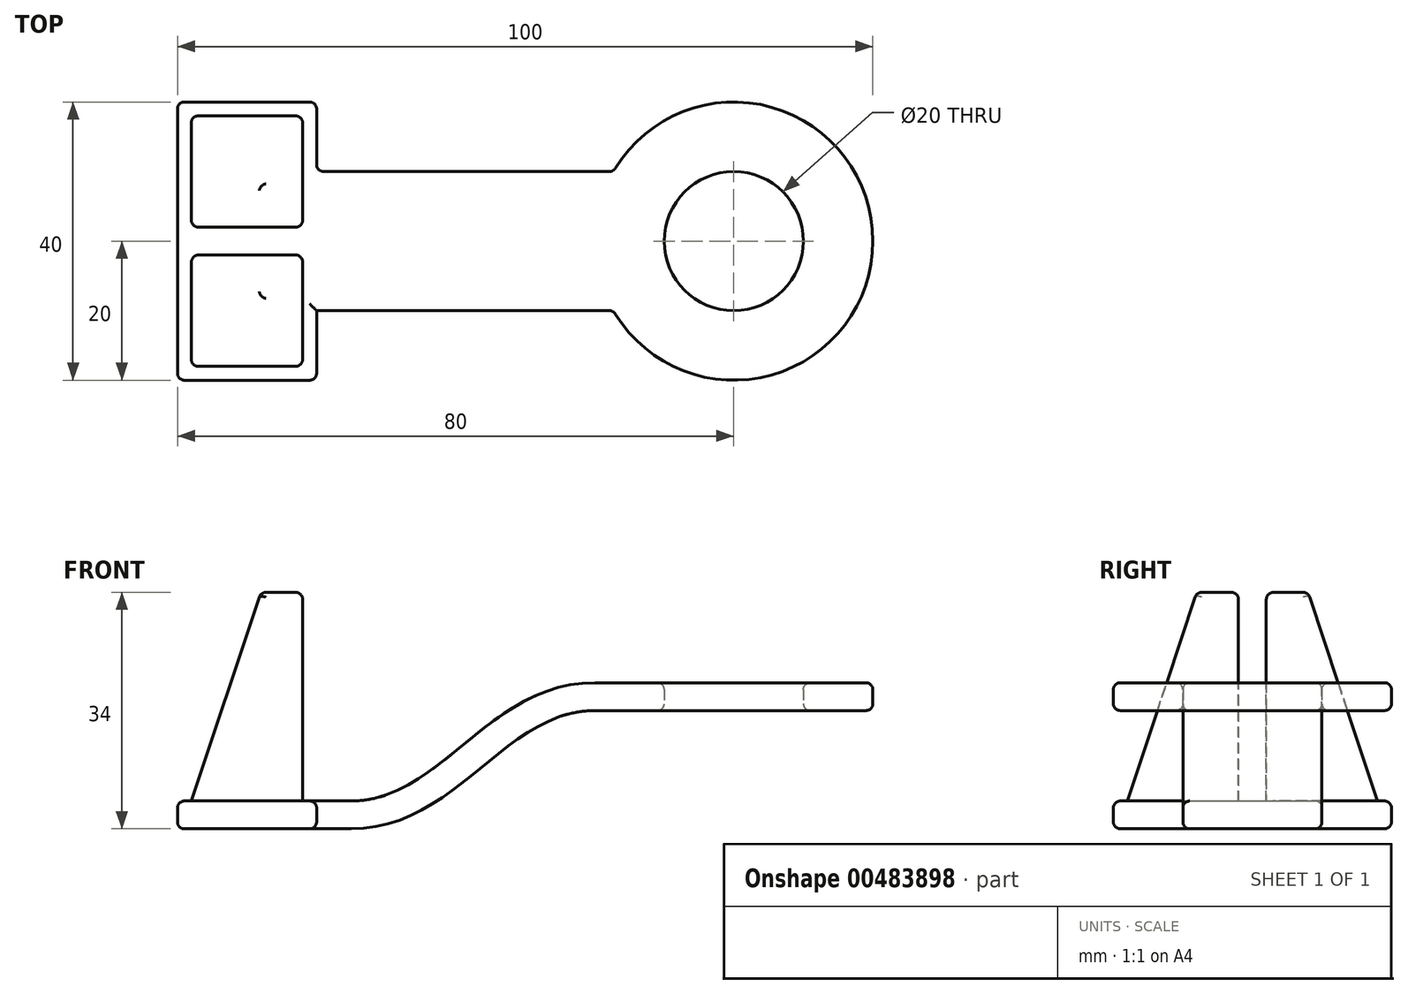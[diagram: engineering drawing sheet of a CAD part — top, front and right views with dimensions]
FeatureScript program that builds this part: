
annotation { "Feature Type Name" : "Feature", "Feature Type Description" : "" }
export const myFeature = defineFeature(function(context is Context, id is Id, definition is map)
    precondition{}
    {
        {
            var Q0;
            Q0=qCreatedBy(makeId("Front.planeOp"),FACE);
            var sketch = newSketch(context, id + "F0", { "sketchPlane" : qUnion([Q0])});
            skLineSegment(sketch, "E0.bottom", {"start": v(10, -2) * mm, "end": v(-10, -2) * mm});
            skLineSegment(sketch, "E0.top", {"start": v(10, 2) * mm, "end": v(-10, 2) * mm});
            skLineSegment(sketch, "E0.left", {"start": v(10, -2) * mm, "end": v(10, 2) * mm});
            skLineSegment(sketch, "E0.right", {"start": v(-10, -2) * mm, "end": v(-10, 2) * mm});
            skPoint(sketch, "E0.middle", {"position": v(0, 0) * mm});
            skLineSegment(sketch, "E1.bottom", {"start": v(56, 15) * mm, "end": v(50, 15) * mm});
            skLineSegment(sketch, "E1.top", {"start": v(56, 19) * mm, "end": v(50, 19) * mm});
            skLineSegment(sketch, "E1.left", {"start": v(56, 15) * mm, "end": v(56, 19) * mm});
            skLineSegment(sketch, "E1.right", {"start": v(50, 15) * mm, "end": v(50, 19) * mm});
            skPoint(sketch, "E1.middle", {"position": v(53, 17) * mm});
            skLineSegment(sketch, "E2.0", {"start": v(70, 15) * mm, "end": v(70, 19) * mm, "construction": true});
            skLineSegment(sketch, "E3.bottom", {"start": v(80, 15) * mm, "end": v(90, 15) * mm});
            skLineSegment(sketch, "E3.top", {"start": v(80, 19) * mm, "end": v(90, 19) * mm});
            skLineSegment(sketch, "E3.left", {"start": v(80, 15) * mm, "end": v(80, 19) * mm});
            skLineSegment(sketch, "E3.right", {"start": v(90, 15) * mm, "end": v(90, 19) * mm});
            skLineSegment(sketch, "E4.bottom", {"start": v(10, -2) * mm, "end": v(15, -2) * mm});
            skLineSegment(sketch, "E4.top", {"start": v(10, 2) * mm, "end": v(15, 2) * mm});
            skLineSegment(sketch, "E4.right", {"start": v(15, -2) * mm, "end": v(15, 2) * mm});
            skFitSpline(sketch, "E5", {"points": [v(15, 2) * mm, v(50, 19) * mm], "startDerivative": vector(38.92, 0) * mm, "endDerivative": vector(46.09, 0) * mm});
            skFitSpline(sketch, "E6", {"points": [v(15, -2) * mm, v(50, 15) * mm], "startDerivative": vector(45.29, 0) * mm, "endDerivative": vector(38.92, 0) * mm});
            skSolve(sketch);
        }
        {
            var Q0;
            Q0=makeQuery(id+"F0.imprint","IMPRINT",FACE,{"disambiguationData":[TD([[makeQuery(id+"F0.imprint","IMPRINT",EDGE,{"derivedFrom":sQuery(id+"F0.wireOp",EDGE,"E3.bottom")}),1.0]])]});
            var Q1;
            Q1=sQuery(id+"F0.wireOp",EDGE,"E2.0");
            revolve(context, id + "F1", {"entities" : qUnion([Q0]), "axis" : qUnion([Q1]), "revolveType" : RevolveType.FULL});
        }
        {
            var Q0;
            Q0=makeQuery(id+"F0.imprint","IMPRINT",FACE,{"disambiguationData":[TD([[makeQuery(id+"F0.imprint","IMPRINT",EDGE,{"derivedFrom":sQuery(id+"F0.wireOp",EDGE,"E1.bottom")}),-1.0]])]});
            extrude(context, id + "F2", {"entities" : qUnion([Q0]), "operationType" : NewBodyOperationType.ADD, "endBound" : BoundingType.SYMMETRIC, "depth" : 20 * mm, "offsetDistance" : 25 * mm});
        }
        {
            var Q0;
            Q0=makeQuery(id+"F0.imprint","IMPRINT",FACE,{"disambiguationData":[TD([[makeQuery(id+"F0.imprint","IMPRINT",EDGE,{"derivedFrom":sQuery(id+"F0.wireOp",EDGE,"E0.bottom")}),-1.0]])]});
            extrude(context, id + "F3", {"entities" : qUnion([Q0]), "operationType" : NewBodyOperationType.ADD, "endBound" : BoundingType.SYMMETRIC, "depth" : 40 * mm, "offsetDistance" : 25 * mm});
        }
        {
            var Q0;
            Q0=makeQuery(id+"F0.imprint","IMPRINT",FACE,{"disambiguationData":[TD([[makeQuery(id+"F0.imprint","IMPRINT",EDGE,{"derivedFrom":sQuery(id+"F0.wireOp",EDGE,"E1.right")}),1.0]])]});
            extrude(context, id + "F4", {"entities" : qUnion([Q0]), "operationType" : NewBodyOperationType.ADD, "endBound" : BoundingType.SYMMETRIC, "depth" : 20 * mm, "offsetDistance" : 25 * mm});
        }
        {
            var Q0;
            Q0=makeQuery(id+"F0.imprint","IMPRINT",FACE,{"disambiguationData":[TD([[makeQuery(id+"F0.imprint","IMPRINT",EDGE,{"derivedFrom":sQuery(id+"F0.wireOp",EDGE,"E4.bottom")}),1.0]])]});
            extrude(context, id + "F5", {"entities" : qUnion([Q0]), "operationType" : NewBodyOperationType.ADD, "endBound" : BoundingType.SYMMETRIC, "depth" : 20 * mm, "offsetDistance" : 25 * mm});
        }
        {
            var Q0;
            Q0=makeQuery(id+"F3.opExtrude","SWEPT_FACE",FACE,{"disambiguationData":[OSD([sQuery(id+"F0.wireOp",EDGE,"E0.top")])]});
            var sketch = newSketch(context, id + "F6", { "sketchPlane" : qUnion([Q0])});
            skLineSegment(sketch, "E7.bottom", {"start": v(-8, 18) * mm, "end": v(8, 18) * mm});
            skLineSegment(sketch, "E7.top", {"start": v(-8, 2) * mm, "end": v(8, 2) * mm});
            skLineSegment(sketch, "E7.left", {"start": v(-8, 18) * mm, "end": v(-8, 2) * mm});
            skLineSegment(sketch, "E7.right", {"start": v(8, 18) * mm, "end": v(8, 2) * mm});
            skLineSegment(sketch, "E8.MirrorCS", {"start": v(-8, -2) * mm, "end": v(8, -2) * mm});
            skLineSegment(sketch, "E9.MirrorCS", {"start": v(8, -18) * mm, "end": v(8, -2) * mm});
            skLineSegment(sketch, "E10.MirrorCS", {"start": v(-8, -18) * mm, "end": v(8, -18) * mm});
            skLineSegment(sketch, "E11.MirrorCS", {"start": v(-8, -18) * mm, "end": v(-8, -2) * mm});
            skSolve(sketch);
        }
        {
            var Q0;
            Q0=makeQuery(id+"F3.opExtrude","SWEPT_FACE",FACE,{"disambiguationData":[OSD([sQuery(id+"F0.wireOp",EDGE,"E0.top")])]});
            cPlane(context, id + "F7", {"entities" : qUnion([Q0]), "cplaneType" : CPlaneType.OFFSET, "offset" : 30 * mm, "width" : 150 * mm, "height" : 150 * mm});
        }
        {
            var Q0;
            Q0=qCreatedBy(id+"F7.planeOp",FACE);
            var sketch = newSketch(context, id + "F8", { "sketchPlane" : qUnion([Q0])});
            skLineSegment(sketch, "E12.bottom", {"start": v(8, 2) * mm, "end": v(2, 2) * mm});
            skLineSegment(sketch, "E12.top", {"start": v(8, 8) * mm, "end": v(2, 8) * mm});
            skLineSegment(sketch, "E12.left", {"start": v(2, 8) * mm, "end": v(2, 2) * mm});
            skLineSegment(sketch, "E12.right", {"start": v(8, 8) * mm, "end": v(8, 2) * mm});
            skLineSegment(sketch, "E13.MirrorCS", {"start": v(8, -2) * mm, "end": v(2, -2) * mm});
            skLineSegment(sketch, "E14.MirrorCS", {"start": v(8, -8) * mm, "end": v(8, -2) * mm});
            skLineSegment(sketch, "E15.MirrorCS", {"start": v(8, -8) * mm, "end": v(2, -8) * mm});
            skLineSegment(sketch, "E16.MirrorCS", {"start": v(2, -8) * mm, "end": v(2, -2) * mm});
            skSolve(sketch);
        }
        {
            var Q1;
            Q1=makeQuery(id+"F6.imprint","IMPRINT",FACE,{"disambiguationData":[TD([[makeQuery(id+"F6.imprint","IMPRINT",EDGE,{"derivedFrom":sQuery(id+"F6.wireOp",EDGE,"E8.MirrorCS")}),-1.0]])]});
            var Q2;
            Q2=makeQuery(id+"F8.imprint","IMPRINT",FACE,{"disambiguationData":[TD([[makeQuery(id+"F8.imprint","IMPRINT",EDGE,{"derivedFrom":sQuery(id+"F8.wireOp",EDGE,"E13.MirrorCS")}),1.0]])]});
            loft(context, id + "F9", {"operationType" : NewBodyOperationType.ADD, "sheetProfilesArray" : [{ "sheetProfileEntities" : qUnion([Q1]) }, { "sheetProfileEntities" : qUnion([Q2]) }]});
        }
        {
            var Q1;
            Q1=makeQuery(id+"F6.imprint","IMPRINT",FACE,{"disambiguationData":[TD([[makeQuery(id+"F6.imprint","IMPRINT",EDGE,{"derivedFrom":sQuery(id+"F6.wireOp",EDGE,"E7.bottom")}),-1.0]])]});
            var Q2;
            Q2=makeQuery(id+"F8.imprint","IMPRINT",FACE,{"disambiguationData":[TD([[makeQuery(id+"F8.imprint","IMPRINT",EDGE,{"derivedFrom":sQuery(id+"F8.wireOp",EDGE,"E12.bottom")}),-1.0]])]});
            loft(context, id + "F10", {"operationType" : NewBodyOperationType.ADD, "sheetProfilesArray" : [{ "sheetProfileEntities" : qUnion([Q1]) }, { "sheetProfileEntities" : qUnion([Q2]) }]});
        }
        {
            var Q0;
            Q0=makeQuery(id+"F3.opExtrude","CAP_EDGE",EDGE,{"disambiguationData":[OSD([sQuery(id+"F0.wireOp",EDGE,"E0.bottom")])],"isStart":false});
            var Q1;
            Q1=makeQuery(id+"F3.opExtrude","SWEPT_EDGE",EDGE,{"disambiguationData":[OSD([sQuery(id+"F0.wireOp",EDGE,"E0.bottom"),sQuery(id+"F0.wireOp",EDGE,"E0.right")])]});
            var Q2;
            Q2=makeQuery(id+"F3.opExtrude","CAP_EDGE",EDGE,{"disambiguationData":[OSD([sQuery(id+"F0.wireOp",EDGE,"E0.bottom")])],"isStart":true});
            var Q3;
            {var subQ0=sQuery(id+"F0.wireOp",EDGE,"E0.left");var subQ1=sQuery(id+"F0.wireOp",EDGE,"E0.bottom");var subQ2=sQuery(id+"F0.wireOp",EDGE,"E1.right");var subQ4=sQuery(id+"F0.wireOp",EDGE,"E4.bottom");Q3=makeQuery(id+"F5.boolean.opBoolean","SPLIT",EDGE,{"disambiguationData":[TD([makeQuery(id+"F2.opExtrude","CAP_FACE",FACE,{"disambiguationData":[OSD([sQuery(id+"F0.wireOp",EDGE,"E1.bottom"),sQuery(id+"F0.wireOp",EDGE,"E1.top"),sQuery(id+"F0.wireOp",EDGE,"E1.left"),subQ2])],"isStart":true})])],"derivedFrom":makeQuery(id+"F3.opExtrude","SWEPT_EDGE",EDGE,{"disambiguationData":[OSD([subQ1,subQ4,subQ0])]})});}
            var Q4;
            {var subQ0=sQuery(id+"F0.wireOp",EDGE,"E0.left");var subQ1=sQuery(id+"F0.wireOp",EDGE,"E0.bottom");var subQ2=sQuery(id+"F0.wireOp",EDGE,"E1.right");var subQ4=sQuery(id+"F0.wireOp",EDGE,"E4.bottom");Q4=makeQuery(id+"F5.boolean.opBoolean","SPLIT",EDGE,{"disambiguationData":[TD([makeQuery(id+"F2.opExtrude","CAP_FACE",FACE,{"disambiguationData":[OSD([sQuery(id+"F0.wireOp",EDGE,"E1.bottom"),sQuery(id+"F0.wireOp",EDGE,"E1.top"),sQuery(id+"F0.wireOp",EDGE,"E1.left"),subQ2])],"isStart":false})])],"derivedFrom":makeQuery(id+"F3.opExtrude","SWEPT_EDGE",EDGE,{"disambiguationData":[OSD([subQ1,subQ4,subQ0])]})});}
            fillet(context, id + "F11", {"entities" : qUnion([Q0, Q1, Q2, Q3, Q4]), "radius" : 1 * mm, "tangentPropagation" : true, "allowEdgeOverflow" : false});
        }
        {
            var Q0;
            Q0=makeQuery(id+"F3.opExtrude","CAP_EDGE",EDGE,{"disambiguationData":[OSD([sQuery(id+"F0.wireOp",EDGE,"E0.top")])],"isStart":false});
            var Q1;
            {var subQ0=sQuery(id+"F0.wireOp",EDGE,"E0.top");var subQ2=sQuery(id+"F0.wireOp",EDGE,"E1.right");var subQ3=sQuery(id+"F0.wireOp",EDGE,"E0.left");var subQ4=sQuery(id+"F0.wireOp",EDGE,"E4.top");Q1=makeQuery(id+"F5.boolean.opBoolean","SPLIT",EDGE,{"disambiguationData":[TD([makeQuery(id+"F2.opExtrude","CAP_FACE",FACE,{"disambiguationData":[OSD([sQuery(id+"F0.wireOp",EDGE,"E1.bottom"),sQuery(id+"F0.wireOp",EDGE,"E1.top"),sQuery(id+"F0.wireOp",EDGE,"E1.left"),subQ2])],"isStart":false})])],"derivedFrom":makeQuery(id+"F3.opExtrude","SWEPT_EDGE",EDGE,{"disambiguationData":[OSD([subQ0,subQ4,subQ3])]})});}
            var Q2;
            Q2=makeQuery(id+"F3.opExtrude","SWEPT_EDGE",EDGE,{"disambiguationData":[OSD([sQuery(id+"F0.wireOp",EDGE,"E0.top"),sQuery(id+"F0.wireOp",EDGE,"E0.right")])]});
            var Q3;
            Q3=makeQuery(id+"F5.opExtrude","CAP_EDGE",EDGE,{"disambiguationData":[OSD([sQuery(id+"F0.wireOp",EDGE,"E4.top")])],"isStart":false});
            var Q4;
            Q4=makeQuery(id+"F5.opExtrude","CAP_EDGE",EDGE,{"disambiguationData":[OSD([sQuery(id+"F0.wireOp",EDGE,"E4.top")])],"isStart":true});
            var Q5;
            {var subQ0=sQuery(id+"F0.wireOp",EDGE,"E0.left");var subQ1=sQuery(id+"F0.wireOp",EDGE,"E0.top");var subQ2=sQuery(id+"F0.wireOp",EDGE,"E4.top");var subQ3=sQuery(id+"F0.wireOp",EDGE,"E1.right");Q5=makeQuery(id+"F5.boolean.opBoolean","SPLIT",EDGE,{"disambiguationData":[TD([makeQuery(id+"F2.opExtrude","CAP_FACE",FACE,{"disambiguationData":[OSD([sQuery(id+"F0.wireOp",EDGE,"E1.bottom"),sQuery(id+"F0.wireOp",EDGE,"E1.top"),sQuery(id+"F0.wireOp",EDGE,"E1.left"),subQ3])],"isStart":true})])],"derivedFrom":makeQuery(id+"F3.opExtrude","SWEPT_EDGE",EDGE,{"disambiguationData":[OSD([subQ1,subQ2,subQ0])]})});}
            var Q6;
            Q6=makeQuery(id+"F3.opExtrude","CAP_EDGE",EDGE,{"disambiguationData":[OSD([sQuery(id+"F0.wireOp",EDGE,"E0.top")])],"isStart":true});
            var Q7;
            Q7=makeQuery(id+"F3.opExtrude","CAP_EDGE",EDGE,{"disambiguationData":[OSD([sQuery(id+"F0.wireOp",EDGE,"E0.left")])],"isStart":false});
            var Q8;
            Q8=makeQuery(id+"F3.opExtrude","CAP_EDGE",EDGE,{"disambiguationData":[OSD([sQuery(id+"F0.wireOp",EDGE,"E0.right")])],"isStart":false});
            var Q9;
            Q9=makeQuery(id+"F3.opExtrude","CAP_EDGE",EDGE,{"disambiguationData":[OSD([sQuery(id+"F0.wireOp",EDGE,"E0.left")])],"isStart":true});
            var Q10;
            Q10=makeQuery(id+"F5.opExtrude","CAP_EDGE",EDGE,{"disambiguationData":[OSD([sQuery(id+"F0.wireOp",EDGE,"E4.bottom")])],"isStart":false});
            var Q11;
            Q11=makeQuery(id+"F5.opExtrude","CAP_EDGE",EDGE,{"disambiguationData":[OSD([sQuery(id+"F0.wireOp",EDGE,"E0.left")])],"isStart":false});
            var Q12;
            Q12=makeQuery(id+"F3.opExtrude","CAP_EDGE",EDGE,{"disambiguationData":[OSD([sQuery(id+"F0.wireOp",EDGE,"E0.right")])],"isStart":true});
            var Q13;
            Q13=makeQuery(id+"F5.opExtrude","CAP_EDGE",EDGE,{"disambiguationData":[OSD([sQuery(id+"F0.wireOp",EDGE,"E0.left")])],"isStart":true});
            var Q14;
            Q14=makeQuery(id+"F5.opExtrude","CAP_EDGE",EDGE,{"disambiguationData":[OSD([sQuery(id+"F0.wireOp",EDGE,"E4.bottom")])],"isStart":true});
            fillet(context, id + "F12", {"entities" : qUnion([Q0, Q1, Q2, Q3, Q4, Q5, Q6, Q7, Q8, Q9, Q10, Q11, Q12, Q13, Q14]), "radius" : 1 * mm, "tangentPropagation" : true, "allowEdgeOverflow" : false});
        }
        {
            var Q0;
            Q0=makeQuery(id+"F9.opLoft","MID_CAP_EDGE",EDGE,{"disambiguationData":[OSD([sQuery(id+"F6.wireOp",EDGE,"E9.MirrorCS"),sQuery(id+"F6.wireOp",EDGE,"E10.MirrorCS"),sQuery(id+"F6.wireOp",EDGE,"E11.MirrorCS")])],"capPos":0.0});
            var Q1;
            Q1=makeQuery(id+"F9.opLoft","SWEPT_EDGE",EDGE,{"disambiguationData":[OSD([sQuery(id+"F6.wireOp",EDGE,"E10.MirrorCS"),sQuery(id+"F6.wireOp",EDGE,"E11.MirrorCS"),sQuery(id+"F8.wireOp",EDGE,"E15.MirrorCS"),sQuery(id+"F8.wireOp",EDGE,"E16.MirrorCS")])]});
            var Q2;
            Q2=makeQuery(id+"F9.opLoft","SWEPT_EDGE",EDGE,{"disambiguationData":[OSD([sQuery(id+"F6.wireOp",EDGE,"E9.MirrorCS"),sQuery(id+"F6.wireOp",EDGE,"E10.MirrorCS"),sQuery(id+"F8.wireOp",EDGE,"E14.MirrorCS"),sQuery(id+"F8.wireOp",EDGE,"E15.MirrorCS")])]});
            var Q3;
            Q3=makeQuery(id+"F9.opLoft","MID_CAP_EDGE",EDGE,{"disambiguationData":[OSD([sQuery(id+"F6.wireOp",EDGE,"E8.MirrorCS"),sQuery(id+"F6.wireOp",EDGE,"E9.MirrorCS"),sQuery(id+"F6.wireOp",EDGE,"E10.MirrorCS")])],"capPos":0.0});
            var Q4;
            Q4=makeQuery(id+"F9.opLoft","SWEPT_EDGE",EDGE,{"disambiguationData":[OSD([sQuery(id+"F6.wireOp",EDGE,"E8.MirrorCS"),sQuery(id+"F6.wireOp",EDGE,"E9.MirrorCS"),sQuery(id+"F8.wireOp",EDGE,"E13.MirrorCS"),sQuery(id+"F8.wireOp",EDGE,"E14.MirrorCS")])]});
            var Q5;
            Q5=makeQuery(id+"F9.opLoft","MID_CAP_EDGE",EDGE,{"disambiguationData":[OSD([sQuery(id+"F8.wireOp",EDGE,"E13.MirrorCS"),sQuery(id+"F8.wireOp",EDGE,"E14.MirrorCS"),sQuery(id+"F8.wireOp",EDGE,"E15.MirrorCS")])],"capPos":1.0});
            var Q6;
            Q6=makeQuery(id+"F9.opLoft","MID_CAP_EDGE",EDGE,{"disambiguationData":[OSD([sQuery(id+"F8.wireOp",EDGE,"E14.MirrorCS"),sQuery(id+"F8.wireOp",EDGE,"E15.MirrorCS"),sQuery(id+"F8.wireOp",EDGE,"E16.MirrorCS")])],"capPos":1.0});
            var Q7;
            Q7=makeQuery(id+"F9.opLoft","MID_CAP_EDGE",EDGE,{"disambiguationData":[OSD([sQuery(id+"F8.wireOp",EDGE,"E13.MirrorCS"),sQuery(id+"F8.wireOp",EDGE,"E15.MirrorCS"),sQuery(id+"F8.wireOp",EDGE,"E16.MirrorCS")])],"capPos":1.0});
            var Q8;
            Q8=makeQuery(id+"F9.opLoft","MID_CAP_EDGE",EDGE,{"disambiguationData":[OSD([sQuery(id+"F8.wireOp",EDGE,"E13.MirrorCS"),sQuery(id+"F8.wireOp",EDGE,"E14.MirrorCS"),sQuery(id+"F8.wireOp",EDGE,"E16.MirrorCS")])],"capPos":1.0});
            var Q9;
            Q9=makeQuery(id+"F10.opLoft","MID_CAP_EDGE",EDGE,{"disambiguationData":[OSD([sQuery(id+"F8.wireOp",EDGE,"E12.bottom"),sQuery(id+"F8.wireOp",EDGE,"E12.left"),sQuery(id+"F8.wireOp",EDGE,"E12.right")])],"capPos":1.0});
            var Q10;
            Q10=makeQuery(id+"F10.opLoft","SWEPT_EDGE",EDGE,{"disambiguationData":[OSD([sQuery(id+"F6.wireOp",EDGE,"E7.top"),sQuery(id+"F6.wireOp",EDGE,"E7.right"),sQuery(id+"F8.wireOp",EDGE,"E12.bottom"),sQuery(id+"F8.wireOp",EDGE,"E12.right")])]});
            var Q11;
            Q11=makeQuery(id+"F10.opLoft","MID_CAP_EDGE",EDGE,{"disambiguationData":[OSD([sQuery(id+"F8.wireOp",EDGE,"E12.bottom"),sQuery(id+"F8.wireOp",EDGE,"E12.top"),sQuery(id+"F8.wireOp",EDGE,"E12.right")])],"capPos":1.0});
            var Q12;
            Q12=makeQuery(id+"F10.opLoft","SWEPT_EDGE",EDGE,{"disambiguationData":[OSD([sQuery(id+"F6.wireOp",EDGE,"E7.bottom"),sQuery(id+"F6.wireOp",EDGE,"E7.right"),sQuery(id+"F8.wireOp",EDGE,"E12.top"),sQuery(id+"F8.wireOp",EDGE,"E12.right")])]});
            var Q13;
            Q13=makeQuery(id+"F10.opLoft","MID_CAP_EDGE",EDGE,{"disambiguationData":[OSD([sQuery(id+"F6.wireOp",EDGE,"E7.bottom"),sQuery(id+"F6.wireOp",EDGE,"E7.top"),sQuery(id+"F6.wireOp",EDGE,"E7.right")])],"capPos":0.0});
            var Q14;
            Q14=makeQuery(id+"F10.opLoft","SWEPT_EDGE",EDGE,{"disambiguationData":[OSD([sQuery(id+"F6.wireOp",EDGE,"E7.top"),sQuery(id+"F6.wireOp",EDGE,"E7.left"),sQuery(id+"F8.wireOp",EDGE,"E12.bottom"),sQuery(id+"F8.wireOp",EDGE,"E12.left")])]});
            var Q15;
            Q15=makeQuery(id+"F10.opLoft","MID_CAP_EDGE",EDGE,{"disambiguationData":[OSD([sQuery(id+"F6.wireOp",EDGE,"E7.bottom"),sQuery(id+"F6.wireOp",EDGE,"E7.top"),sQuery(id+"F6.wireOp",EDGE,"E7.left")])],"capPos":0.0});
            var Q16;
            Q16=makeQuery(id+"F9.opLoft","SWEPT_EDGE",EDGE,{"disambiguationData":[OSD([sQuery(id+"F6.wireOp",EDGE,"E8.MirrorCS"),sQuery(id+"F6.wireOp",EDGE,"E11.MirrorCS"),sQuery(id+"F8.wireOp",EDGE,"E13.MirrorCS"),sQuery(id+"F8.wireOp",EDGE,"E16.MirrorCS")])]});
            var Q17;
            Q17=makeQuery(id+"F10.opLoft","MID_CAP_EDGE",EDGE,{"disambiguationData":[OSD([sQuery(id+"F8.wireOp",EDGE,"E12.bottom"),sQuery(id+"F8.wireOp",EDGE,"E12.top"),sQuery(id+"F8.wireOp",EDGE,"E12.left")])],"capPos":1.0});
            var Q18;
            Q18=makeQuery(id+"F10.opLoft","SWEPT_EDGE",EDGE,{"disambiguationData":[OSD([sQuery(id+"F6.wireOp",EDGE,"E7.bottom"),sQuery(id+"F6.wireOp",EDGE,"E7.left"),sQuery(id+"F8.wireOp",EDGE,"E12.top"),sQuery(id+"F8.wireOp",EDGE,"E12.left")])]});
            var Q19;
            Q19=makeQuery(id+"F10.opLoft","MID_CAP_EDGE",EDGE,{"disambiguationData":[OSD([sQuery(id+"F8.wireOp",EDGE,"E12.top"),sQuery(id+"F8.wireOp",EDGE,"E12.left"),sQuery(id+"F8.wireOp",EDGE,"E12.right")])],"capPos":1.0});
            fillet(context, id + "F13", {"entities" : qUnion([Q0, Q1, Q2, Q3, Q4, Q5, Q6, Q7, Q8, Q9, Q10, Q11, Q12, Q13, Q14, Q15, Q16, Q17, Q18, Q19]), "radius" : 1 * mm, "tangentPropagation" : true, "allowEdgeOverflow" : false});
        }
        {
            var Q0;
            Q0=makeQuery(id+"F1.opRevolve","SWEPT_EDGE",EDGE,{"disambiguationData":[OSD([sQuery(id+"F0.wireOp",EDGE,"E3.top"),sQuery(id+"F0.wireOp",EDGE,"E3.right")])]});
            var Q1;
            Q1=makeQuery(id+"F1.opRevolve","SWEPT_EDGE",EDGE,{"disambiguationData":[OSD([sQuery(id+"F0.wireOp",EDGE,"E3.bottom"),sQuery(id+"F0.wireOp",EDGE,"E3.right")])]});
            var Q2;
            Q2=makeQuery(id+"F2.boolean.opBoolean","INTERSECT",EDGE,{"derivedFrom":[makeQuery(id+"F1.opRevolve","SWEPT_FACE",FACE,{"disambiguationData":[OSD([sQuery(id+"F0.wireOp",EDGE,"E3.right")])]}),makeQuery(id+"F2.opExtrude","CAP_FACE",FACE,{"disambiguationData":[OSD([sQuery(id+"F0.wireOp",EDGE,"E1.bottom"),sQuery(id+"F0.wireOp",EDGE,"E1.top"),sQuery(id+"F0.wireOp",EDGE,"E1.left"),sQuery(id+"F0.wireOp",EDGE,"E1.right")])],"isStart":true})]});
            var Q3;
            Q3=makeQuery(id+"F2.boolean.opBoolean","INTERSECT",EDGE,{"derivedFrom":[makeQuery(id+"F1.opRevolve","SWEPT_FACE",FACE,{"disambiguationData":[OSD([sQuery(id+"F0.wireOp",EDGE,"E3.right")])]}),makeQuery(id+"F2.opExtrude","CAP_FACE",FACE,{"disambiguationData":[OSD([sQuery(id+"F0.wireOp",EDGE,"E1.bottom"),sQuery(id+"F0.wireOp",EDGE,"E1.top"),sQuery(id+"F0.wireOp",EDGE,"E1.left"),sQuery(id+"F0.wireOp",EDGE,"E1.right")])],"isStart":false})]});
            var Q4;
            Q4=makeQuery(id+"F1.opRevolve","SWEPT_EDGE",EDGE,{"disambiguationData":[OSD([sQuery(id+"F0.wireOp",EDGE,"E3.bottom"),sQuery(id+"F0.wireOp",EDGE,"E3.left")])]});
            var Q5;
            Q5=makeQuery(id+"F1.opRevolve","SWEPT_EDGE",EDGE,{"disambiguationData":[OSD([sQuery(id+"F0.wireOp",EDGE,"E3.top"),sQuery(id+"F0.wireOp",EDGE,"E3.left")])]});
            fillet(context, id + "F14", {"entities" : qUnion([Q0, Q1, Q2, Q3, Q4, Q5]), "radius" : 1 * mm, "tangentPropagation" : true, "allowEdgeOverflow" : false});
        }
    });
